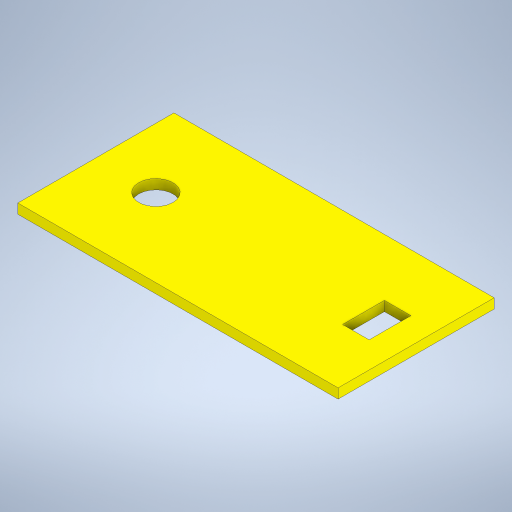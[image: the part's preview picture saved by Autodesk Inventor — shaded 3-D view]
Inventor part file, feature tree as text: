
AUTODESK INVENTOR PART (.ipt)
format: ipt  version: 2024 (Build 280153000, 153)  size: 239,616 bytes
history: native  units: mm
features: extrude x3, sketch x3
ambient origin geometry x8: Origin, YZ Plane, XZ Plane, XY Plane, X Axis, Y Axis, Z Axis, Center Point
bodies: Solid1 (feature_tree)
feature tree (6):
  extrude  "Extrusion1"  Depth=50.0mm
  extrude  "Extrusion2"  Depth=3.125mm
  extrude  "Extrusion3"  Depth=8.5mm
  sketch  "Sketch1"  dims[d0=102.6mm d1=50.0mm]
  sketch  "Sketch2"  dims[d2=3.125mm d3=0.0mm d4=11.0mm]
  sketch  "Sketch3"  dims[d5=3.125mm d6=0.0mm d7=8.5mm d8=13.4mm d9=3.125mm d10=0.0mm]
